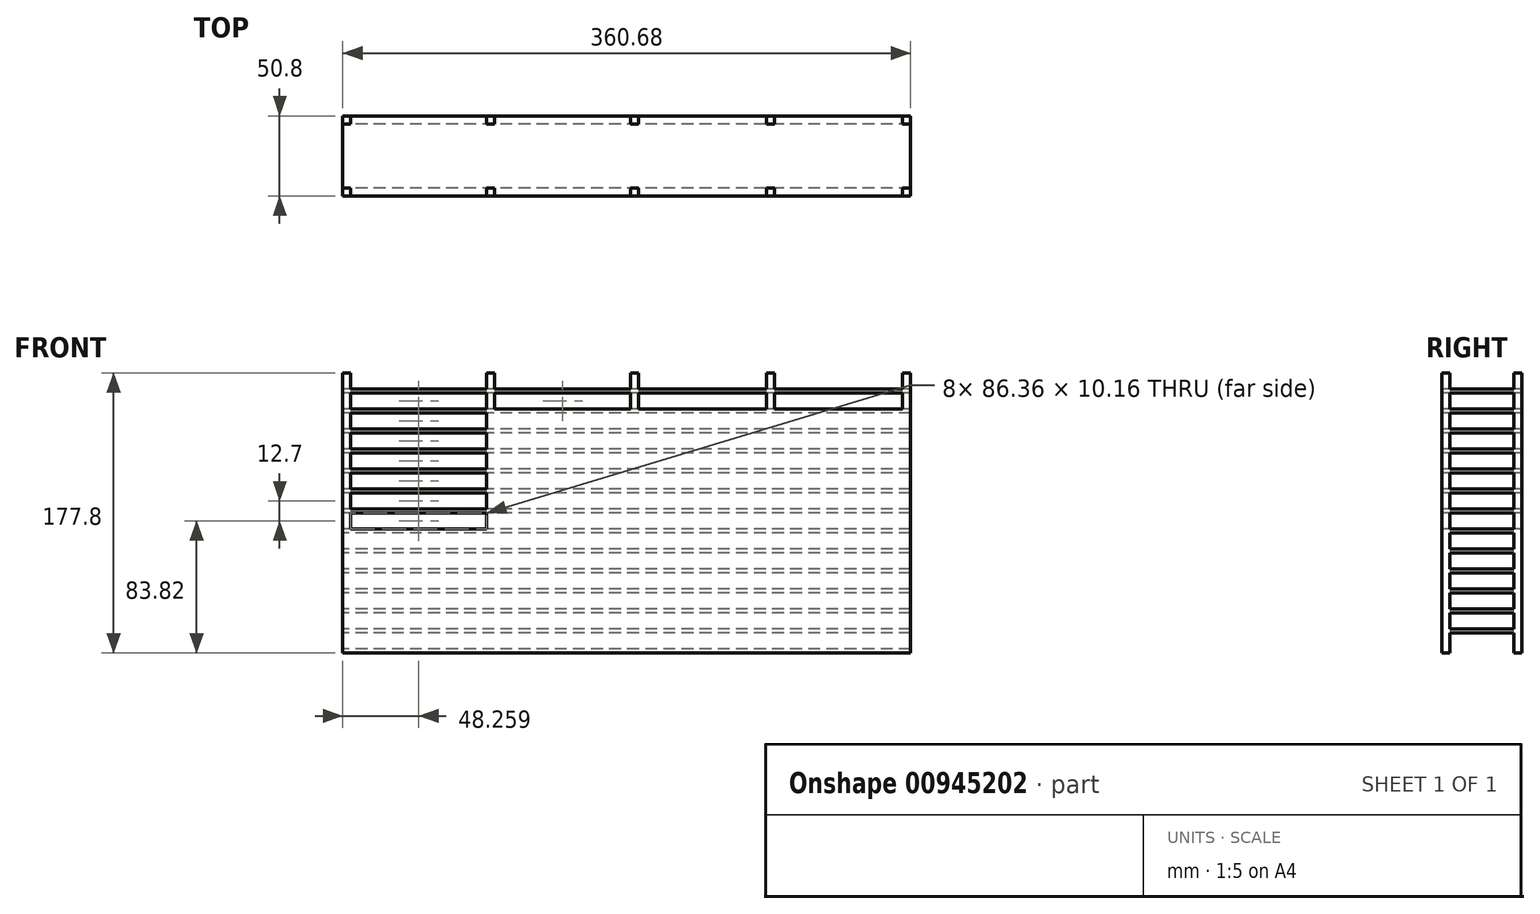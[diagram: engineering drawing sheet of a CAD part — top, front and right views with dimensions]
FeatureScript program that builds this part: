
annotation { "Feature Type Name" : "Feature", "Feature Type Description" : "" }
export const myFeature = defineFeature(function(context is Context, id is Id, definition is map)
    precondition{}
    {
        {
            var Q0;
            Q0=qCreatedBy(makeId("Top.planeOp"),FACE);
            var sketch = newSketch(context, id + "F0", { "sketchPlane" : qUnion([Q0])});
            skLineSegment(sketch, "E0.bottom", {"start": v(-304, 42.04) * mm, "end": v(56.69, 42.04) * mm});
            skLineSegment(sketch, "E0.top", {"start": v(-304, -8.76) * mm, "end": v(56.69, -8.76) * mm});
            skLineSegment(sketch, "E0.left", {"start": v(-304, 42.04) * mm, "end": v(-304, -8.76) * mm});
            skLineSegment(sketch, "E0.right", {"start": v(56.69, 42.04) * mm, "end": v(56.69, -8.76) * mm});
            skSolve(sketch);
        }
        {
            var Q0;
            Q0=makeQuery(id+"F0.imprint","IMPRINT",FACE,{"disambiguationData":[TD([[makeQuery(id+"F0.imprint","IMPRINT",EDGE,{"derivedFrom":sQuery(id+"F0.wireOp",EDGE,"E0.bottom")}),-1.0]])]});
            extrude(context, id + "F1", {"entities" : qUnion([Q0]), "depth" : 177.8 * mm, "offsetDistance" : 25.4 * mm});
        }
        {
            var Q0;
            Q0=makeQuery(id+"F1.opExtrude","SWEPT_FACE",FACE,{"disambiguationData":[OSD([sQuery(id+"F0.wireOp",EDGE,"E0.left")])]});
            var sketch = newSketch(context, id + "F2", { "sketchPlane" : qUnion([Q0])});
            skLineSegment(sketch, "E1.bottom", {"start": v(-42.04, 177.8) * mm, "end": v(-36.96, 177.8) * mm});
            skLineSegment(sketch, "E1.top", {"start": v(-42.04, 0) * mm, "end": v(-36.96, 0) * mm});
            skLineSegment(sketch, "E1.left", {"start": v(-42.04, 177.8) * mm, "end": v(-42.04, 0) * mm});
            skLineSegment(sketch, "E1.right", {"start": v(-36.96, 177.8) * mm, "end": v(-36.96, 0) * mm});
            skLineSegment(sketch, "E2.bottom", {"start": v(8.76, 177.8) * mm, "end": v(3.68, 177.8) * mm});
            skLineSegment(sketch, "E2.top", {"start": v(8.76, 0) * mm, "end": v(3.68, 0) * mm});
            skLineSegment(sketch, "E2.left", {"start": v(8.76, 177.8) * mm, "end": v(8.76, 0) * mm});
            skLineSegment(sketch, "E2.right", {"start": v(3.68, 177.8) * mm, "end": v(3.68, 0) * mm});
            skLineSegment(sketch, "E3.bottom", {"start": v(-36.96, 177.8) * mm, "end": v(3.68, 177.8) * mm});
            skLineSegment(sketch, "E3.top", {"start": v(-36.96, 167.64) * mm, "end": v(3.68, 167.64) * mm});
            skLineSegment(sketch, "E3.left", {"start": v(-36.96, 177.8) * mm, "end": v(-36.96, 167.64) * mm});
            skLineSegment(sketch, "E3.right", {"start": v(3.68, 177.8) * mm, "end": v(3.68, 167.64) * mm});
            skLineSegment(sketch, "E4.top", {"start": v(-36.96, 165.1) * mm, "end": v(3.68, 165.1) * mm});
            skLineSegment(sketch, "E4.left", {"start": v(-36.96, 167.64) * mm, "end": v(-36.96, 165.1) * mm});
            skLineSegment(sketch, "E4.right", {"start": v(3.68, 167.64) * mm, "end": v(3.68, 165.1) * mm});
            skLineSegment(sketch, "E5.top", {"start": v(-36.96, 154.94) * mm, "end": v(3.68, 154.94) * mm});
            skLineSegment(sketch, "E5.left", {"start": v(-36.96, 165.1) * mm, "end": v(-36.96, 154.94) * mm});
            skLineSegment(sketch, "E5.right", {"start": v(3.68, 165.1) * mm, "end": v(3.68, 154.94) * mm});
            skLineSegment(sketch, "E6.bottom", {"start": v(3.68, 154.94) * mm, "end": v(-36.96, 154.94) * mm});
            skLineSegment(sketch, "E6.top", {"start": v(3.68, 152.4) * mm, "end": v(-36.96, 152.4) * mm});
            skLineSegment(sketch, "E6.left", {"start": v(3.68, 154.94) * mm, "end": v(3.68, 152.4) * mm});
            skLineSegment(sketch, "E6.right", {"start": v(-36.96, 154.94) * mm, "end": v(-36.96, 152.4) * mm});
            skLineSegment(sketch, "E7.bottom", {"start": v(-36.96, 152.4) * mm, "end": v(3.68, 152.4) * mm});
            skLineSegment(sketch, "E7.top", {"start": v(-36.96, 142.24) * mm, "end": v(3.68, 142.24) * mm});
            skLineSegment(sketch, "E7.left", {"start": v(-36.96, 152.4) * mm, "end": v(-36.96, 142.24) * mm});
            skLineSegment(sketch, "E7.right", {"start": v(3.68, 152.4) * mm, "end": v(3.68, 142.24) * mm});
            skLineSegment(sketch, "E8.bottom", {"start": v(3.68, 142.24) * mm, "end": v(-36.96, 142.24) * mm});
            skLineSegment(sketch, "E8.top", {"start": v(3.68, 139.7) * mm, "end": v(-36.96, 139.7) * mm});
            skLineSegment(sketch, "E8.left", {"start": v(3.68, 142.24) * mm, "end": v(3.68, 139.7) * mm});
            skLineSegment(sketch, "E8.right", {"start": v(-36.96, 142.24) * mm, "end": v(-36.96, 139.7) * mm});
            skLineSegment(sketch, "E9.bottom", {"start": v(-36.96, 139.7) * mm, "end": v(3.68, 139.7) * mm});
            skLineSegment(sketch, "E9.top", {"start": v(-36.96, 129.54) * mm, "end": v(3.68, 129.54) * mm});
            skLineSegment(sketch, "E9.left", {"start": v(-36.96, 139.7) * mm, "end": v(-36.96, 129.54) * mm});
            skLineSegment(sketch, "E9.right", {"start": v(3.68, 139.7) * mm, "end": v(3.68, 129.54) * mm});
            skLineSegment(sketch, "E10.bottom", {"start": v(3.68, 129.54) * mm, "end": v(-36.96, 129.54) * mm});
            skLineSegment(sketch, "E10.top", {"start": v(3.68, 127) * mm, "end": v(-36.96, 127) * mm});
            skLineSegment(sketch, "E10.left", {"start": v(3.68, 129.54) * mm, "end": v(3.68, 127) * mm});
            skLineSegment(sketch, "E10.right", {"start": v(-36.96, 129.54) * mm, "end": v(-36.96, 127) * mm});
            skLineSegment(sketch, "E11.bottom", {"start": v(-36.96, 127) * mm, "end": v(3.68, 127) * mm});
            skLineSegment(sketch, "E11.top", {"start": v(-36.96, 116.84) * mm, "end": v(3.68, 116.84) * mm});
            skLineSegment(sketch, "E11.left", {"start": v(-36.96, 127) * mm, "end": v(-36.96, 116.84) * mm});
            skLineSegment(sketch, "E11.right", {"start": v(3.68, 127) * mm, "end": v(3.68, 116.84) * mm});
            skLineSegment(sketch, "E12.bottom", {"start": v(3.68, 116.84) * mm, "end": v(-36.96, 116.84) * mm});
            skLineSegment(sketch, "E12.top", {"start": v(3.68, 114.3) * mm, "end": v(-36.96, 114.3) * mm});
            skLineSegment(sketch, "E12.left", {"start": v(3.68, 116.84) * mm, "end": v(3.68, 114.3) * mm});
            skLineSegment(sketch, "E12.right", {"start": v(-36.96, 116.84) * mm, "end": v(-36.96, 114.3) * mm});
            skLineSegment(sketch, "E13.bottom", {"start": v(-36.96, 114.3) * mm, "end": v(3.68, 114.3) * mm});
            skLineSegment(sketch, "E13.top", {"start": v(-36.96, 104.14) * mm, "end": v(3.68, 104.14) * mm});
            skLineSegment(sketch, "E13.left", {"start": v(-36.96, 114.3) * mm, "end": v(-36.96, 104.14) * mm});
            skLineSegment(sketch, "E13.right", {"start": v(3.68, 114.3) * mm, "end": v(3.68, 104.14) * mm});
            skLineSegment(sketch, "E14.top", {"start": v(-36.96, 101.6) * mm, "end": v(3.68, 101.6) * mm});
            skLineSegment(sketch, "E14.left", {"start": v(-36.96, 104.14) * mm, "end": v(-36.96, 101.6) * mm});
            skLineSegment(sketch, "E14.right", {"start": v(3.68, 104.14) * mm, "end": v(3.68, 101.6) * mm});
            skLineSegment(sketch, "E15.top", {"start": v(-36.96, 91.44) * mm, "end": v(3.68, 91.44) * mm});
            skLineSegment(sketch, "E15.left", {"start": v(-36.96, 101.6) * mm, "end": v(-36.96, 91.44) * mm});
            skLineSegment(sketch, "E15.right", {"start": v(3.68, 101.6) * mm, "end": v(3.68, 91.44) * mm});
            skLineSegment(sketch, "E16.top", {"start": v(-36.96, 88.9) * mm, "end": v(3.68, 88.9) * mm});
            skLineSegment(sketch, "E16.left", {"start": v(-36.96, 91.44) * mm, "end": v(-36.96, 88.9) * mm});
            skLineSegment(sketch, "E16.right", {"start": v(3.68, 91.44) * mm, "end": v(3.68, 88.9) * mm});
            skLineSegment(sketch, "E17.bottom", {"start": v(3.68, 88.9) * mm, "end": v(-36.96, 88.9) * mm});
            skLineSegment(sketch, "E17.top", {"start": v(3.68, 78.74) * mm, "end": v(-36.96, 78.74) * mm});
            skLineSegment(sketch, "E17.left", {"start": v(3.68, 88.9) * mm, "end": v(3.68, 78.74) * mm});
            skLineSegment(sketch, "E17.right", {"start": v(-36.96, 88.9) * mm, "end": v(-36.96, 78.74) * mm});
            skLineSegment(sketch, "E18.top", {"start": v(3.68, 76.2) * mm, "end": v(-36.96, 76.2) * mm});
            skLineSegment(sketch, "E18.left", {"start": v(3.68, 78.74) * mm, "end": v(3.68, 76.2) * mm});
            skLineSegment(sketch, "E18.right", {"start": v(-36.96, 78.74) * mm, "end": v(-36.96, 76.2) * mm});
            skLineSegment(sketch, "E19.bottom", {"start": v(-36.96, 76.2) * mm, "end": v(3.68, 76.2) * mm});
            skLineSegment(sketch, "E19.top", {"start": v(-36.96, 66.04) * mm, "end": v(3.68, 66.04) * mm});
            skLineSegment(sketch, "E19.left", {"start": v(-36.96, 76.2) * mm, "end": v(-36.96, 66.04) * mm});
            skLineSegment(sketch, "E19.right", {"start": v(3.68, 76.2) * mm, "end": v(3.68, 66.04) * mm});
            skLineSegment(sketch, "E20.top", {"start": v(-36.96, 63.5) * mm, "end": v(3.68, 63.5) * mm});
            skLineSegment(sketch, "E20.left", {"start": v(-36.96, 66.04) * mm, "end": v(-36.96, 63.5) * mm});
            skLineSegment(sketch, "E20.right", {"start": v(3.68, 66.04) * mm, "end": v(3.68, 63.5) * mm});
            skLineSegment(sketch, "E21.top", {"start": v(-36.96, 60.96) * mm, "end": v(3.68, 60.96) * mm});
            skLineSegment(sketch, "E21.left", {"start": v(-36.96, 63.5) * mm, "end": v(-36.96, 60.96) * mm});
            skLineSegment(sketch, "E21.right", {"start": v(3.68, 63.5) * mm, "end": v(3.68, 60.96) * mm});
            skLineSegment(sketch, "E22.top", {"start": v(-36.96, 53.34) * mm, "end": v(3.68, 53.34) * mm});
            skLineSegment(sketch, "E22.left", {"start": v(-36.96, 63.5) * mm, "end": v(-36.96, 53.34) * mm});
            skLineSegment(sketch, "E22.right", {"start": v(3.68, 63.5) * mm, "end": v(3.68, 53.34) * mm});
            skLineSegment(sketch, "E23.top", {"start": v(-36.96, 50.8) * mm, "end": v(3.68, 50.8) * mm});
            skLineSegment(sketch, "E23.left", {"start": v(-36.96, 53.34) * mm, "end": v(-36.96, 50.8) * mm});
            skLineSegment(sketch, "E23.right", {"start": v(3.68, 53.34) * mm, "end": v(3.68, 50.8) * mm});
            skLineSegment(sketch, "E24.top", {"start": v(-36.96, 40.64) * mm, "end": v(3.68, 40.64) * mm});
            skLineSegment(sketch, "E24.left", {"start": v(-36.96, 50.8) * mm, "end": v(-36.96, 40.64) * mm});
            skLineSegment(sketch, "E24.right", {"start": v(3.68, 50.8) * mm, "end": v(3.68, 40.64) * mm});
            skLineSegment(sketch, "E25.top", {"start": v(-36.96, 38.1) * mm, "end": v(3.68, 38.1) * mm});
            skLineSegment(sketch, "E25.left", {"start": v(-36.96, 40.64) * mm, "end": v(-36.96, 38.1) * mm});
            skLineSegment(sketch, "E25.right", {"start": v(3.68, 40.64) * mm, "end": v(3.68, 38.1) * mm});
            skLineSegment(sketch, "E26.bottom", {"start": v(3.68, 38.1) * mm, "end": v(-36.96, 38.1) * mm});
            skLineSegment(sketch, "E26.top", {"start": v(3.68, 27.94) * mm, "end": v(-36.96, 27.94) * mm});
            skLineSegment(sketch, "E26.left", {"start": v(3.68, 38.1) * mm, "end": v(3.68, 27.94) * mm});
            skLineSegment(sketch, "E26.right", {"start": v(-36.96, 38.1) * mm, "end": v(-36.96, 27.94) * mm});
            skLineSegment(sketch, "E27.top", {"start": v(3.68, 25.4) * mm, "end": v(-36.96, 25.4) * mm});
            skLineSegment(sketch, "E27.left", {"start": v(3.68, 27.94) * mm, "end": v(3.68, 25.4) * mm});
            skLineSegment(sketch, "E27.right", {"start": v(-36.96, 27.94) * mm, "end": v(-36.96, 25.4) * mm});
            skLineSegment(sketch, "E28.top", {"start": v(3.68, 15.24) * mm, "end": v(-36.96, 15.24) * mm});
            skLineSegment(sketch, "E28.left", {"start": v(3.68, 25.4) * mm, "end": v(3.68, 15.24) * mm});
            skLineSegment(sketch, "E28.right", {"start": v(-36.96, 25.4) * mm, "end": v(-36.96, 15.24) * mm});
            skLineSegment(sketch, "E29.top", {"start": v(3.68, 12.7) * mm, "end": v(-36.96, 12.7) * mm});
            skLineSegment(sketch, "E29.left", {"start": v(3.68, 15.24) * mm, "end": v(3.68, 12.7) * mm});
            skLineSegment(sketch, "E29.right", {"start": v(-36.96, 15.24) * mm, "end": v(-36.96, 12.7) * mm});
            skLineSegment(sketch, "E30.bottom", {"start": v(-36.96, 12.7) * mm, "end": v(3.68, 12.7) * mm});
            skLineSegment(sketch, "E30.top", {"start": v(-36.96, 2.54) * mm, "end": v(3.68, 2.54) * mm});
            skLineSegment(sketch, "E30.left", {"start": v(-36.96, 12.7) * mm, "end": v(-36.96, 2.54) * mm});
            skLineSegment(sketch, "E30.right", {"start": v(3.68, 12.7) * mm, "end": v(3.68, 2.54) * mm});
            skSolve(sketch);
        }
        {
            var Q0;
            {var subQ0=sQuery(id+"F2.wireOp",EDGE,"E29.top");Q0=makeQuery(id+"F2.imprint","IMPRINT",FACE,{"disambiguationData":[TD([[makeQuery(id+"F2.imprint","IMPRINT",EDGE,{"derivedFrom":subQ0}),1.0]])]});}
            var Q1;
            {var subQ0=sQuery(id+"F2.wireOp",EDGE,"E27.top");Q1=makeQuery(id+"F2.imprint","IMPRINT",FACE,{"disambiguationData":[TD([[makeQuery(id+"F2.imprint","IMPRINT",EDGE,{"derivedFrom":subQ0}),1.0]])]});}
            var Q2;
            {var subQ0=sQuery(id+"F2.wireOp",EDGE,"E25.top");Q2=makeQuery(id+"F2.imprint","IMPRINT",FACE,{"disambiguationData":[TD([[makeQuery(id+"F2.imprint","IMPRINT",EDGE,{"derivedFrom":subQ0}),-1.0]])]});}
            var Q3;
            {var subQ0=sQuery(id+"F2.wireOp",EDGE,"E23.top");Q3=makeQuery(id+"F2.imprint","IMPRINT",FACE,{"disambiguationData":[TD([[makeQuery(id+"F2.imprint","IMPRINT",EDGE,{"derivedFrom":subQ0}),-1.0]])]});}
            var Q4;
            {var subQ0=sQuery(id+"F2.wireOp",EDGE,"E21.top");Q4=makeQuery(id+"F2.imprint","IMPRINT",FACE,{"disambiguationData":[TD([[makeQuery(id+"F2.imprint","IMPRINT",EDGE,{"derivedFrom":subQ0}),-1.0]])]});}
            var Q5;
            {var subQ0=sQuery(id+"F2.wireOp",EDGE,"E20.top");Q5=makeQuery(id+"F2.imprint","IMPRINT",FACE,{"disambiguationData":[TD([[makeQuery(id+"F2.imprint","IMPRINT",EDGE,{"derivedFrom":subQ0}),-1.0]])]});}
            var Q6;
            {var subQ0=sQuery(id+"F2.wireOp",EDGE,"E18.top");Q6=makeQuery(id+"F2.imprint","IMPRINT",FACE,{"disambiguationData":[TD([[makeQuery(id+"F2.imprint","IMPRINT",EDGE,{"derivedFrom":subQ0}),1.0]])]});}
            var Q7;
            {var subQ0=sQuery(id+"F2.wireOp",EDGE,"E16.top");Q7=makeQuery(id+"F2.imprint","IMPRINT",FACE,{"disambiguationData":[TD([[makeQuery(id+"F2.imprint","IMPRINT",EDGE,{"derivedFrom":subQ0}),-1.0]])]});}
            var Q8;
            {var subQ0=sQuery(id+"F2.wireOp",EDGE,"E14.top");Q8=makeQuery(id+"F2.imprint","IMPRINT",FACE,{"disambiguationData":[TD([[makeQuery(id+"F2.imprint","IMPRINT",EDGE,{"derivedFrom":subQ0}),-1.0]])]});}
            var Q9;
            {var subQ0=sQuery(id+"F2.wireOp",EDGE,"E12.top");Q9=makeQuery(id+"F2.imprint","IMPRINT",FACE,{"disambiguationData":[TD([[makeQuery(id+"F2.imprint","IMPRINT",EDGE,{"derivedFrom":subQ0}),1.0]])]});}
            var Q10;
            {var subQ0=sQuery(id+"F2.wireOp",EDGE,"E10.top");Q10=makeQuery(id+"F2.imprint","IMPRINT",FACE,{"disambiguationData":[TD([[makeQuery(id+"F2.imprint","IMPRINT",EDGE,{"derivedFrom":subQ0}),1.0]])]});}
            var Q11;
            {var subQ0=sQuery(id+"F2.wireOp",EDGE,"E8.top");Q11=makeQuery(id+"F2.imprint","IMPRINT",FACE,{"disambiguationData":[TD([[makeQuery(id+"F2.imprint","IMPRINT",EDGE,{"derivedFrom":subQ0}),1.0]])]});}
            var Q12;
            {var subQ0=sQuery(id+"F2.wireOp",EDGE,"E6.top");Q12=makeQuery(id+"F2.imprint","IMPRINT",FACE,{"disambiguationData":[TD([[makeQuery(id+"F2.imprint","IMPRINT",EDGE,{"derivedFrom":subQ0}),1.0]])]});}
            var Q13;
            {var subQ0=sQuery(id+"F2.wireOp",EDGE,"E4.top");Q13=makeQuery(id+"F2.imprint","IMPRINT",FACE,{"disambiguationData":[TD([[makeQuery(id+"F2.imprint","IMPRINT",EDGE,{"derivedFrom":subQ0}),-1.0]])]});}
            var Q14;
            {var subQ0=sQuery(id+"F2.wireOp",EDGE,"E3.bottom");Q14=makeQuery(id+"F2.imprint","IMPRINT",FACE,{"disambiguationData":[TD([[makeQuery(id+"F2.imprint","IMPRINT",EDGE,{"derivedFrom":subQ0}),-1.0]])]});}
            extrude(context, id + "F3", {"entities" : qUnion([Q0, Q1, Q2, Q3, Q4, Q5, Q6, Q7, Q8, Q9, Q10, Q11, Q12, Q13, Q14]), "operationType" : NewBodyOperationType.REMOVE, "endBound" : BoundingType.THROUGH_ALL, "oppositeDirection" : true, "depth" : 25.4 * mm, "offsetDistance" : 25.4 * mm});
        }
        {
            var Q0;
            Q0=makeQuery(id+"F1.opExtrude","SWEPT_FACE",FACE,{"disambiguationData":[OSD([sQuery(id+"F0.wireOp",EDGE,"E0.top")])]});
            var sketch = newSketch(context, id + "F4", { "sketchPlane" : qUnion([Q0])});
            skLineSegment(sketch, "E31.bottom", {"start": v(-304, 177.8) * mm, "end": v(-298.91, 177.8) * mm});
            skLineSegment(sketch, "E31.top", {"start": v(-304, 0) * mm, "end": v(-298.91, 0) * mm});
            skLineSegment(sketch, "E31.left", {"start": v(-304, 177.8) * mm, "end": v(-304, 0) * mm});
            skLineSegment(sketch, "E31.right", {"start": v(-298.91, 177.8) * mm, "end": v(-298.91, 0) * mm});
            skLineSegment(sketch, "E32.bottom", {"start": v(56.69, 177.8) * mm, "end": v(51.6, 177.8) * mm});
            skLineSegment(sketch, "E32.top", {"start": v(56.69, 0) * mm, "end": v(51.6, 0) * mm});
            skLineSegment(sketch, "E32.left", {"start": v(56.69, 177.8) * mm, "end": v(56.69, 0) * mm});
            skLineSegment(sketch, "E32.right", {"start": v(51.6, 177.8) * mm, "end": v(51.6, 0) * mm});
            skLineSegment(sketch, "E33.bottom", {"start": v(51.6, 177.8) * mm, "end": v(-34.75, 177.8) * mm});
            skLineSegment(sketch, "E33.top", {"start": v(51.6, 0) * mm, "end": v(-34.75, 0) * mm});
            skLineSegment(sketch, "E33.right", {"start": v(-34.75, 177.8) * mm, "end": v(-34.75, 0) * mm});
            skLineSegment(sketch, "E34.bottom", {"start": v(-34.75, 177.8) * mm, "end": v(-121.11, 177.8) * mm});
            skLineSegment(sketch, "E34.top", {"start": v(-34.75, 0) * mm, "end": v(-121.11, 0) * mm});
            skLineSegment(sketch, "E34.right", {"start": v(-121.11, 177.8) * mm, "end": v(-121.11, 0) * mm});
            skLineSegment(sketch, "E35.bottom", {"start": v(-121.11, 177.8) * mm, "end": v(-207.47, 177.8) * mm});
            skLineSegment(sketch, "E35.top", {"start": v(-121.11, 0) * mm, "end": v(-207.47, 0) * mm});
            skLineSegment(sketch, "E35.right", {"start": v(-207.47, 177.8) * mm, "end": v(-207.47, 0) * mm});
            skLineSegment(sketch, "E36.bottom", {"start": v(-298.91, 177.8) * mm, "end": v(-207.47, 177.8) * mm});
            skLineSegment(sketch, "E36.top", {"start": v(-298.91, 0) * mm, "end": v(-207.47, 0) * mm});
            skLineSegment(sketch, "E37.bottom", {"start": v(-212.55, 177.8) * mm, "end": v(-207.47, 177.8) * mm});
            skLineSegment(sketch, "E37.top", {"start": v(-212.55, 0) * mm, "end": v(-207.47, 0) * mm});
            skLineSegment(sketch, "E37.left", {"start": v(-212.55, 177.8) * mm, "end": v(-212.55, 0) * mm});
            skLineSegment(sketch, "E38.bottom", {"start": v(-121.11, 177.8) * mm, "end": v(-116.03, 177.8) * mm});
            skLineSegment(sketch, "E38.top", {"start": v(-121.11, 0) * mm, "end": v(-116.03, 0) * mm});
            skLineSegment(sketch, "E38.right", {"start": v(-116.03, 177.8) * mm, "end": v(-116.03, 0) * mm});
            skLineSegment(sketch, "E39.bottom", {"start": v(-34.75, 177.8) * mm, "end": v(-29.67, 177.8) * mm});
            skLineSegment(sketch, "E39.top", {"start": v(-34.75, 0) * mm, "end": v(-29.67, 0) * mm});
            skLineSegment(sketch, "E39.right", {"start": v(-29.67, 177.8) * mm, "end": v(-29.67, 0) * mm});
            skLineSegment(sketch, "E40.bottom", {"start": v(-298.91, 177.8) * mm, "end": v(-212.55, 177.8) * mm});
            skLineSegment(sketch, "E40.top", {"start": v(-298.91, 167.64) * mm, "end": v(-212.55, 167.64) * mm});
            skLineSegment(sketch, "E40.left", {"start": v(-298.91, 177.8) * mm, "end": v(-298.91, 167.64) * mm});
            skLineSegment(sketch, "E40.right", {"start": v(-212.55, 177.8) * mm, "end": v(-212.55, 167.64) * mm});
            skLineSegment(sketch, "E41.bottom", {"start": v(-207.47, 177.8) * mm, "end": v(-121.11, 177.8) * mm});
            skLineSegment(sketch, "E41.top", {"start": v(-207.47, 167.64) * mm, "end": v(-121.11, 167.64) * mm});
            skLineSegment(sketch, "E41.left", {"start": v(-207.47, 177.8) * mm, "end": v(-207.47, 167.64) * mm});
            skLineSegment(sketch, "E41.right", {"start": v(-121.11, 177.8) * mm, "end": v(-121.11, 167.64) * mm});
            skLineSegment(sketch, "E42.bottom", {"start": v(-116.03, 177.8) * mm, "end": v(-34.75, 177.8) * mm});
            skLineSegment(sketch, "E42.top", {"start": v(-116.03, 167.64) * mm, "end": v(-34.75, 167.64) * mm});
            skLineSegment(sketch, "E42.left", {"start": v(-116.03, 177.8) * mm, "end": v(-116.03, 167.64) * mm});
            skLineSegment(sketch, "E42.right", {"start": v(-34.75, 177.8) * mm, "end": v(-34.75, 167.64) * mm});
            skLineSegment(sketch, "E43.bottom", {"start": v(-29.67, 177.8) * mm, "end": v(51.6, 177.8) * mm});
            skLineSegment(sketch, "E43.top", {"start": v(-29.67, 167.64) * mm, "end": v(51.6, 167.64) * mm});
            skLineSegment(sketch, "E43.left", {"start": v(-29.67, 177.8) * mm, "end": v(-29.67, 167.64) * mm});
            skLineSegment(sketch, "E43.right", {"start": v(51.6, 177.8) * mm, "end": v(51.6, 167.64) * mm});
            skLineSegment(sketch, "E44.top", {"start": v(-298.91, 165.1) * mm, "end": v(-212.55, 165.1) * mm});
            skLineSegment(sketch, "E44.left", {"start": v(-298.91, 167.64) * mm, "end": v(-298.91, 165.1) * mm});
            skLineSegment(sketch, "E44.right", {"start": v(-212.55, 167.64) * mm, "end": v(-212.55, 165.1) * mm});
            skLineSegment(sketch, "E45.top", {"start": v(-207.47, 165.1) * mm, "end": v(-121.11, 165.1) * mm});
            skLineSegment(sketch, "E45.left", {"start": v(-207.47, 167.64) * mm, "end": v(-207.47, 165.1) * mm});
            skLineSegment(sketch, "E45.right", {"start": v(-121.11, 167.64) * mm, "end": v(-121.11, 165.1) * mm});
            skLineSegment(sketch, "E46.top", {"start": v(-116.03, 165.1) * mm, "end": v(-34.75, 165.1) * mm});
            skLineSegment(sketch, "E46.left", {"start": v(-116.03, 167.64) * mm, "end": v(-116.03, 165.1) * mm});
            skLineSegment(sketch, "E46.right", {"start": v(-34.75, 167.64) * mm, "end": v(-34.75, 165.1) * mm});
            skLineSegment(sketch, "E47.top", {"start": v(-29.67, 165.1) * mm, "end": v(51.6, 165.1) * mm});
            skLineSegment(sketch, "E47.left", {"start": v(-29.67, 167.64) * mm, "end": v(-29.67, 165.1) * mm});
            skLineSegment(sketch, "E47.right", {"start": v(51.6, 167.64) * mm, "end": v(51.6, 165.1) * mm});
            skLineSegment(sketch, "E48.bottom", {"start": v(51.6, 165.1) * mm, "end": v(-29.67, 165.1) * mm});
            skLineSegment(sketch, "E48.top", {"start": v(51.6, 154.94) * mm, "end": v(-29.67, 154.94) * mm});
            skLineSegment(sketch, "E48.left", {"start": v(51.6, 165.1) * mm, "end": v(51.6, 154.94) * mm});
            skLineSegment(sketch, "E48.right", {"start": v(-29.67, 165.1) * mm, "end": v(-29.67, 154.94) * mm});
            skLineSegment(sketch, "E49.bottom", {"start": v(-34.75, 165.1) * mm, "end": v(-116.03, 165.1) * mm});
            skLineSegment(sketch, "E49.top", {"start": v(-34.75, 154.94) * mm, "end": v(-116.03, 154.94) * mm});
            skLineSegment(sketch, "E49.left", {"start": v(-34.75, 165.1) * mm, "end": v(-34.75, 154.94) * mm});
            skLineSegment(sketch, "E49.right", {"start": v(-116.03, 165.1) * mm, "end": v(-116.03, 154.94) * mm});
            skLineSegment(sketch, "E50.bottom", {"start": v(-121.11, 165.1) * mm, "end": v(-207.47, 165.1) * mm});
            skLineSegment(sketch, "E50.top", {"start": v(-121.11, 154.94) * mm, "end": v(-207.47, 154.94) * mm});
            skLineSegment(sketch, "E50.left", {"start": v(-121.11, 165.1) * mm, "end": v(-121.11, 154.94) * mm});
            skLineSegment(sketch, "E50.right", {"start": v(-207.47, 165.1) * mm, "end": v(-207.47, 154.94) * mm});
            skLineSegment(sketch, "E51.bottom", {"start": v(-212.55, 165.1) * mm, "end": v(-298.91, 165.1) * mm});
            skLineSegment(sketch, "E51.top", {"start": v(-212.55, 154.94) * mm, "end": v(-298.91, 154.94) * mm});
            skLineSegment(sketch, "E51.left", {"start": v(-212.55, 165.1) * mm, "end": v(-212.55, 154.94) * mm});
            skLineSegment(sketch, "E51.right", {"start": v(-298.91, 165.1) * mm, "end": v(-298.91, 154.94) * mm});
            skLineSegment(sketch, "E52.bottom", {"start": v(-298.91, 154.94) * mm, "end": v(-212.55, 154.94) * mm});
            skLineSegment(sketch, "E52.top", {"start": v(-298.91, 152.4) * mm, "end": v(-212.55, 152.4) * mm});
            skLineSegment(sketch, "E52.left", {"start": v(-298.91, 154.94) * mm, "end": v(-298.91, 152.4) * mm});
            skLineSegment(sketch, "E52.right", {"start": v(-212.55, 154.94) * mm, "end": v(-212.55, 152.4) * mm});
            skLineSegment(sketch, "E53.top", {"start": v(-298.91, 142.24) * mm, "end": v(-212.55, 142.24) * mm});
            skLineSegment(sketch, "E53.left", {"start": v(-298.91, 152.4) * mm, "end": v(-298.91, 142.24) * mm});
            skLineSegment(sketch, "E53.right", {"start": v(-212.55, 152.4) * mm, "end": v(-212.55, 142.24) * mm});
            skLineSegment(sketch, "E54.top", {"start": v(-298.91, 139.7) * mm, "end": v(-212.55, 139.7) * mm});
            skLineSegment(sketch, "E54.left", {"start": v(-298.91, 142.24) * mm, "end": v(-298.91, 139.7) * mm});
            skLineSegment(sketch, "E54.right", {"start": v(-212.55, 142.24) * mm, "end": v(-212.55, 139.7) * mm});
            skLineSegment(sketch, "E55.top", {"start": v(-298.91, 88.9) * mm, "end": v(-212.55, 88.9) * mm});
            skLineSegment(sketch, "E55.left", {"start": v(-298.91, 139.7) * mm, "end": v(-298.91, 88.9) * mm});
            skLineSegment(sketch, "E55.right", {"start": v(-212.55, 139.7) * mm, "end": v(-212.55, 88.9) * mm});
            skLineSegment(sketch, "E56.top", {"start": v(-298.91, 129.54) * mm, "end": v(-212.55, 129.54) * mm});
            skLineSegment(sketch, "E56.left", {"start": v(-298.91, 139.7) * mm, "end": v(-298.91, 129.54) * mm});
            skLineSegment(sketch, "E56.right", {"start": v(-212.55, 139.7) * mm, "end": v(-212.55, 129.54) * mm});
            skLineSegment(sketch, "E57.top", {"start": v(-298.91, 127) * mm, "end": v(-212.55, 127) * mm});
            skLineSegment(sketch, "E57.left", {"start": v(-298.91, 129.54) * mm, "end": v(-298.91, 127) * mm});
            skLineSegment(sketch, "E57.right", {"start": v(-212.55, 129.54) * mm, "end": v(-212.55, 127) * mm});
            skLineSegment(sketch, "E58.top", {"start": v(-298.91, 116.84) * mm, "end": v(-212.55, 116.84) * mm});
            skLineSegment(sketch, "E58.left", {"start": v(-298.91, 127) * mm, "end": v(-298.91, 116.84) * mm});
            skLineSegment(sketch, "E58.right", {"start": v(-212.55, 127) * mm, "end": v(-212.55, 116.84) * mm});
            skLineSegment(sketch, "E59.top", {"start": v(-298.91, 114.3) * mm, "end": v(-212.55, 114.3) * mm});
            skLineSegment(sketch, "E59.left", {"start": v(-298.91, 116.84) * mm, "end": v(-298.91, 114.3) * mm});
            skLineSegment(sketch, "E59.right", {"start": v(-212.55, 116.84) * mm, "end": v(-212.55, 114.3) * mm});
            skLineSegment(sketch, "E60.bottom", {"start": v(-212.55, 114.3) * mm, "end": v(-298.91, 114.3) * mm});
            skLineSegment(sketch, "E60.top", {"start": v(-212.55, 104.14) * mm, "end": v(-298.91, 104.14) * mm});
            skLineSegment(sketch, "E60.left", {"start": v(-212.55, 114.3) * mm, "end": v(-212.55, 104.14) * mm});
            skLineSegment(sketch, "E60.right", {"start": v(-298.91, 114.3) * mm, "end": v(-298.91, 104.14) * mm});
            skLineSegment(sketch, "E61.top", {"start": v(-212.55, 101.6) * mm, "end": v(-298.91, 101.6) * mm});
            skLineSegment(sketch, "E61.left", {"start": v(-212.55, 104.14) * mm, "end": v(-212.55, 101.6) * mm});
            skLineSegment(sketch, "E61.right", {"start": v(-298.91, 104.14) * mm, "end": v(-298.91, 101.6) * mm});
            skLineSegment(sketch, "E62.top", {"start": v(-212.55, 91.44) * mm, "end": v(-298.91, 91.44) * mm});
            skLineSegment(sketch, "E62.left", {"start": v(-212.55, 101.6) * mm, "end": v(-212.55, 91.44) * mm});
            skLineSegment(sketch, "E62.right", {"start": v(-298.91, 101.6) * mm, "end": v(-298.91, 91.44) * mm});
            skLineSegment(sketch, "E63.top", {"start": v(-212.55, 88.9) * mm, "end": v(-298.91, 88.9) * mm});
            skLineSegment(sketch, "E63.left", {"start": v(-212.55, 91.44) * mm, "end": v(-212.55, 88.9) * mm});
            skLineSegment(sketch, "E63.right", {"start": v(-298.91, 91.44) * mm, "end": v(-298.91, 88.9) * mm});
            skLineSegment(sketch, "E64.top", {"start": v(-298.91, 78.74) * mm, "end": v(-212.55, 78.74) * mm});
            skLineSegment(sketch, "E64.left", {"start": v(-298.91, 88.9) * mm, "end": v(-298.91, 78.74) * mm});
            skLineSegment(sketch, "E64.right", {"start": v(-212.55, 88.9) * mm, "end": v(-212.55, 78.74) * mm});
            skLineSegment(sketch, "E65.top", {"start": v(-298.91, 68.58) * mm, "end": v(-212.55, 68.58) * mm});
            skLineSegment(sketch, "E65.left", {"start": v(-298.91, 78.74) * mm, "end": v(-298.91, 68.58) * mm});
            skLineSegment(sketch, "E65.right", {"start": v(-212.55, 78.74) * mm, "end": v(-212.55, 68.58) * mm});
            skLineSegment(sketch, "E66.top", {"start": v(-298.91, 73.66) * mm, "end": v(-212.55, 73.66) * mm});
            skLineSegment(sketch, "E66.left", {"start": v(-298.91, 78.74) * mm, "end": v(-298.91, 73.66) * mm});
            skLineSegment(sketch, "E66.right", {"start": v(-212.55, 78.74) * mm, "end": v(-212.55, 73.66) * mm});
            skSolve(sketch);
        }
        {
            var Q0;
            {var subQ3=sQuery(id+"F4.wireOp",EDGE,"E40.top");Q0=makeQuery(id+"F4.imprint","IMPRINT",FACE,{"disambiguationData":[TD([[makeQuery(id+"F4.imprint","IMPRINT",EDGE,{"derivedFrom":subQ3}),1.0]])]});}
            var Q1;
            {var subQ0=sQuery(id+"F4.wireOp",EDGE,"E35.bottom");Q1=makeQuery(id+"F4.imprint","IMPRINT",FACE,{"disambiguationData":[TD([[makeQuery(id+"F4.imprint","IMPRINT",EDGE,{"derivedFrom":subQ0}),-1.0]])]});}
            var Q2;
            {var subQ2=sQuery(id+"F4.wireOp",EDGE,"E45.top");Q2=makeQuery(id+"F4.imprint","IMPRINT",FACE,{"disambiguationData":[TD([[makeQuery(id+"F4.imprint","IMPRINT",EDGE,{"derivedFrom":subQ2}),-1.0]])]});}
            var Q3;
            {var subQ3=sQuery(id+"F4.wireOp",EDGE,"E42.top");Q3=makeQuery(id+"F4.imprint","IMPRINT",FACE,{"disambiguationData":[TD([[makeQuery(id+"F4.imprint","IMPRINT",EDGE,{"derivedFrom":subQ3}),1.0]])]});}
            var Q4;
            {var subQ2=sQuery(id+"F4.wireOp",EDGE,"E46.top");Q4=makeQuery(id+"F4.imprint","IMPRINT",FACE,{"disambiguationData":[TD([[makeQuery(id+"F4.imprint","IMPRINT",EDGE,{"derivedFrom":subQ2}),-1.0]])]});}
            var Q5;
            {var subQ3=sQuery(id+"F4.wireOp",EDGE,"E43.top");Q5=makeQuery(id+"F4.imprint","IMPRINT",FACE,{"disambiguationData":[TD([[makeQuery(id+"F4.imprint","IMPRINT",EDGE,{"derivedFrom":subQ3}),1.0]])]});}
            var Q6;
            {var subQ2=sQuery(id+"F4.wireOp",EDGE,"E47.top");Q6=makeQuery(id+"F4.imprint","IMPRINT",FACE,{"disambiguationData":[TD([[makeQuery(id+"F4.imprint","IMPRINT",EDGE,{"derivedFrom":subQ2}),-1.0]])]});}
            var Q7;
            {var subQ0=sQuery(id+"F4.wireOp",EDGE,"E44.top");Q7=makeQuery(id+"F4.imprint","IMPRINT",FACE,{"disambiguationData":[TD([[makeQuery(id+"F4.imprint","IMPRINT",EDGE,{"derivedFrom":subQ0}),-1.0]])]});}
            var Q8;
            {var subQ0=sQuery(id+"F4.wireOp",EDGE,"E52.top");Q8=makeQuery(id+"F4.imprint","IMPRINT",FACE,{"disambiguationData":[TD([[makeQuery(id+"F4.imprint","IMPRINT",EDGE,{"derivedFrom":subQ0}),-1.0]])]});}
            var Q9;
            {var subQ0=sQuery(id+"F4.wireOp",EDGE,"E54.top");Q9=makeQuery(id+"F4.imprint","IMPRINT",FACE,{"disambiguationData":[TD([[makeQuery(id+"F4.imprint","IMPRINT",EDGE,{"derivedFrom":subQ0}),-1.0]])]});}
            var Q10;
            {var subQ0=sQuery(id+"F4.wireOp",EDGE,"E57.top");Q10=makeQuery(id+"F4.imprint","IMPRINT",FACE,{"disambiguationData":[TD([[makeQuery(id+"F4.imprint","IMPRINT",EDGE,{"derivedFrom":subQ0}),-1.0]])]});}
            var Q11;
            {var subQ0=sQuery(id+"F4.wireOp",EDGE,"E59.top");Q11=makeQuery(id+"F4.imprint","IMPRINT",FACE,{"disambiguationData":[TD([[makeQuery(id+"F4.imprint","IMPRINT",EDGE,{"derivedFrom":subQ0}),-1.0]])]});}
            var Q12;
            {var subQ0=sQuery(id+"F4.wireOp",EDGE,"E61.top");Q12=makeQuery(id+"F4.imprint","IMPRINT",FACE,{"disambiguationData":[TD([[makeQuery(id+"F4.imprint","IMPRINT",EDGE,{"derivedFrom":subQ0}),1.0]])]});}
            var Q13;
            {var subQ0=sQuery(id+"F4.wireOp",EDGE,"E55.top");Q13=makeQuery(id+"F4.imprint","IMPRINT",FACE,{"disambiguationData":[TD([[makeQuery(id+"F4.imprint","IMPRINT",EDGE,{"derivedFrom":subQ0}),-1.0]])]});}
            extrude(context, id + "F5", {"entities" : qUnion([Q0, Q1, Q2, Q3, Q4, Q5, Q6, Q7, Q8, Q9, Q10, Q11, Q12, Q13]), "operationType" : NewBodyOperationType.REMOVE, "endBound" : BoundingType.THROUGH_ALL, "oppositeDirection" : true, "depth" : 25.4 * mm, "offsetDistance" : 25.4 * mm});
        }
        {
            var Q0;
            Q0=makeQuery(id+"F1.opExtrude","SWEPT_FACE",FACE,{"disambiguationData":[OSD([sQuery(id+"F0.wireOp",EDGE,"E0.left")])]});
            var sketch = newSketch(context, id + "F6", { "sketchPlane" : qUnion([Q0])});
            skLineSegment(sketch, "E67.bottom", {"start": v(-36.96, 2.54) * mm, "end": v(3.7, 2.54) * mm});
            skLineSegment(sketch, "E67.top", {"start": v(-36.96, 0) * mm, "end": v(3.7, 0) * mm});
            skLineSegment(sketch, "E67.left", {"start": v(-36.96, 2.54) * mm, "end": v(-36.96, 0) * mm});
            skLineSegment(sketch, "E67.right", {"start": v(3.7, 2.54) * mm, "end": v(3.7, 0) * mm});
            skSolve(sketch);
        }
        {
            var Q0;
            Q0=makeQuery(id+"F6.imprint","IMPRINT",FACE,{"disambiguationData":[TD([[makeQuery(id+"F6.imprint","IMPRINT",EDGE,{"derivedFrom":sQuery(id+"F6.wireOp",EDGE,"E67.top")}),1.0]])]});
            extrude(context, id + "F7", {"entities" : qUnion([Q0]), "operationType" : NewBodyOperationType.REMOVE, "endBound" : BoundingType.THROUGH_ALL, "oppositeDirection" : true, "depth" : 25.4 * mm, "offsetDistance" : 25.4 * mm});
        }
    });
